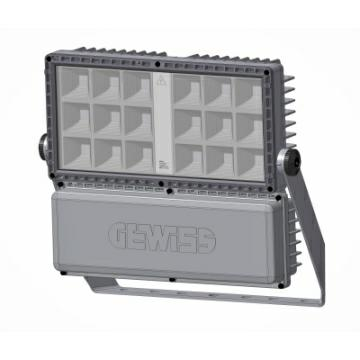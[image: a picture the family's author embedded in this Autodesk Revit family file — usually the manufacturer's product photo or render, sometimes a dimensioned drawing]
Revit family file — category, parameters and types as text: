
# Revit family: Lighting-Proiezione-GEWISS-SMART[PRO]2.0-PROIETTORI-LED-MEDIA-POTENZA_1MODULI_DALI_CLII
name_source: partatom
category: Apparecchi per illuminazione
units: mm (PartAtom-declared; Revit-internal decimal feet)

## family parameters
Condiviso = No
Host = Superficie
Punto di calcolo locali = No
Quota connettore circolare = Usa diametro
Sorgente d'illuminazione = No
Taglio con vuoti quando caricato = No
Tipo di parte = Normale

## types (1)
- Lighting-Proiezione-GEWISS-SMART[PRO]2.0-PROIETTORI-LED-MEDIA-POTENZA_1MODULI_DALI_CLII
    Alimentatore = Incluso
    Apparecchio a ridotta temperatura superficiale = Si
    Applicazione = Interno / Esterno
    Cablaggio = Connettore stagno
    Caratteristiche elettriche e gestione della luce = -
    Caratteristiche ottiche e illuminotecniche = -
    Catalogo = LIGHTING
    Certificazione DIN 18032-3 = Si
    Certificazioni e classificazioni = -
    Classe fotobiologica = -
    Classe isolamento = II
    Classificazione: = -
    Codice digitale univoco (Datamatrix) = Attualmente non presente
    Colore = Grigio grafite
    Contesto = Illuminazione di grandi aree, impianti sportivi
    Controllo abbagliamento e luminanza = G*6 - ULOR = 0
    Corpo = Alluminio pressofuso
    Descrizione = SMARTPRO2.0 1M 4000K CRI80 A3 DALI CL2
    Dispositivo di protezione = DM 6 kV / CM 10 kV
    Durata di vita = L90B10 (Tq+25°C) - 50000h L90B10 (Tq+50°C) = 32000h L80B10 (Tq+25°C) - 110000h
    Efficienza luminosa (lm/W) = 107
    Finitura colore = Verniciato a polvere poliestere
    Fissaggio = Staffa
    Frequenza nominale (Hz) = 50 / 60
    GW - Codice Electrocod = 2424
    Gancio di chiusura = Viti metriche esagonali
    Garanzia = 5 anni
    Grado di protezione = IP66
    Gruppo ottico = Parabola in alluminio anodizzato brillantato con alluminio puro 99,99%
    Guarnizioni = silicone antinvecchiamento
    IDF = d0b7a0d3-4940-475c-a13d-a5bc13a70130
    IDT = 44936a2a5e034791af2c92c80339c9aa
    IPEA = STRADALE = A // GRANDI AREE = A3+ // CICLOPEDONALI = A+ // AREE VERDI = A+ // CENTRO STORICO = A5+ // ALTRO = A5+
    Immagine tipo = SMARTPRO20_1M.jpg
    Inclinazione = Rotazione su staffa con goniometro integrato
    Indice di resa cromatica = CRI-80
    Informazioni generali = -
    Installazione e manutenzione = -
    Lumen output (lm) = 17600
    Materiali = -
    Modello = GWP2184NB
    Norma di riferimento = EN60598-1; EN60598-2-5; EN60598-2-24; IEC 62778; IEC62471; EN13201
    Ottica = A3 - Asimmetrica Stretta
    Peso (kg): = 5,7
    Potenza di sistema = 165W
    Produttore = GEWISS S.p.A.
    Prospetto di default = 1219 mm
    Resistenza agli urti = IK08
    Resistenza al filo incandescente = -
    SEO = Proiettore
    Scheda Tecnica = https://www.gewiss.com
    Schermo = Vetro piano extrachiaro spessore 4mm
    Sistema di controllo = DALI
    Sostituibilità gruppo ottico = Non disponibile
    Sostituibilità piastra di cablaggio = Non disponibile
    Superficie massima esposta al vento : = 0,085 m2
    Temperatura di colore = 4000K
    Temperatura di esercizio = -30 +50 °C
    Temperatura di stoccaggio = -
    Tensione di alimentazione = 220 - 240 V
    Tipo di apparecchio = Apparecchio per proiezione LED di piccola, media e alta potenza
    Tipo di installazione e montaggio = Torrefaro - Parete - Terra
    Tipologia sorgente luminosa = LED - Non sostituibile
    Tolleranza cromatica = SDCM = 3
    URL = https://www.gewiss.com
    Vano di alimentazione = Integrato
    Versione file RFA = 20.11
    Versioni = Luce naturale 4000K
    Viti esterne = Acciaio inossidabile

## geometry (parser evidence)
native form markers: Blend x4
no freeform markers — native parametric forms only
